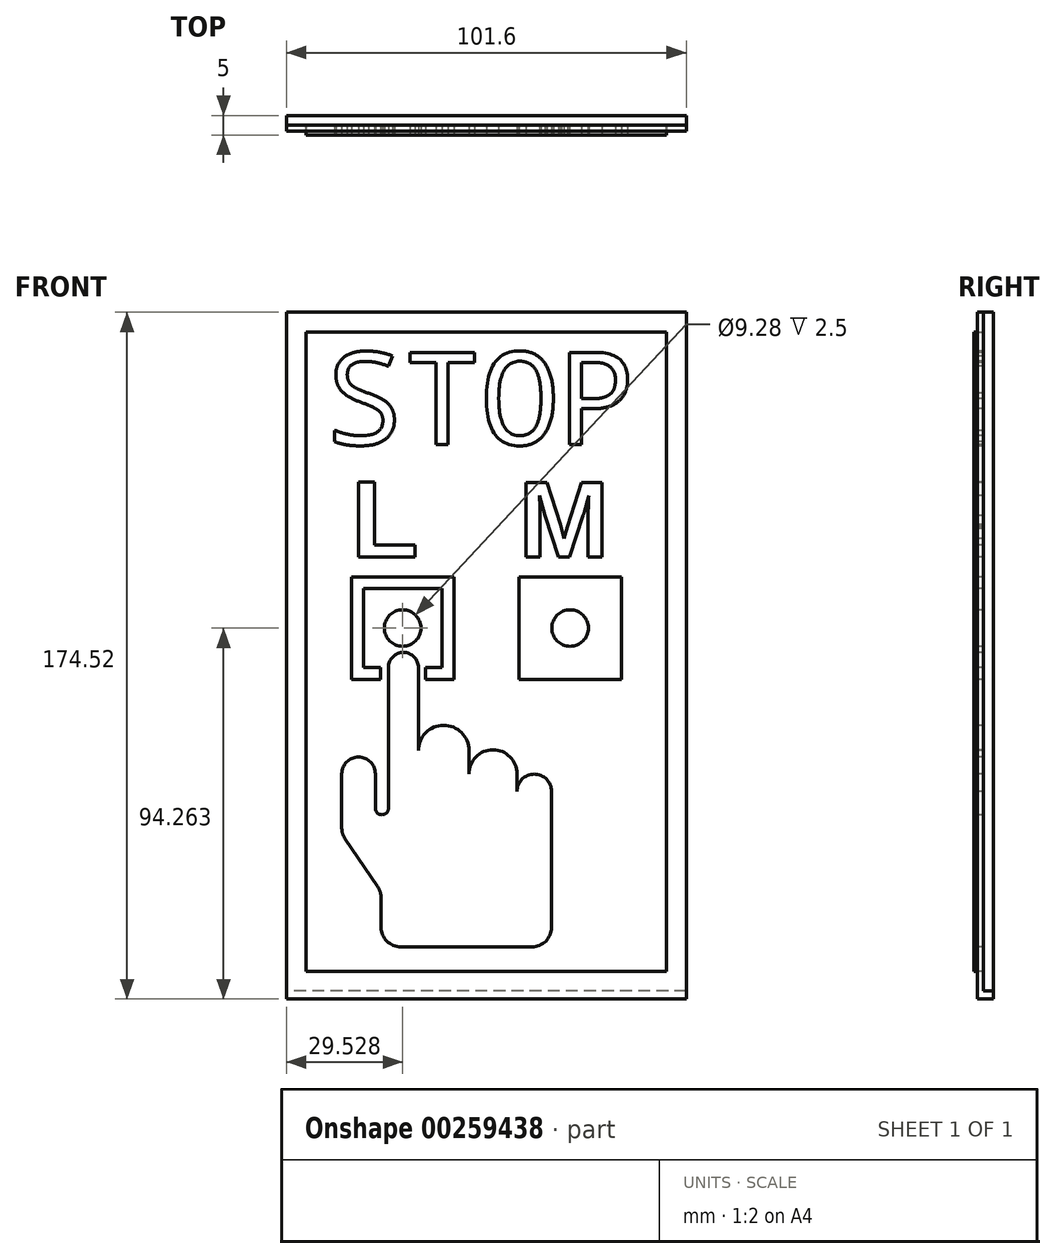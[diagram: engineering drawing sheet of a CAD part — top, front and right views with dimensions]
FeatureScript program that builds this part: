
annotation { "Feature Type Name" : "Feature", "Feature Type Description" : "" }
export const myFeature = defineFeature(function(context is Context, id is Id, definition is map)
    precondition{}
    {
        {
            var Q0;
            Q0=qCreatedBy(makeId("Front.planeOp"),FACE);
            var sketch = newSketch(context, id + "F0", { "sketchPlane" : qUnion([Q0])});
            skLineSegment(sketch, "E0.bottom", {"start": v(0, 0) * mm, "end": v(101.6, 0) * mm});
            skLineSegment(sketch, "E0.top", {"start": v(0, 203.2) * mm, "end": v(101.6, 203.2) * mm});
            skLineSegment(sketch, "E0.left", {"start": v(0, 0) * mm, "end": v(0, 203.2) * mm});
            skLineSegment(sketch, "E0.right", {"start": v(101.6, 0) * mm, "end": v(101.6, 203.2) * mm});
            skLineSegment(sketch, "E1.0", {"start": v(5, 5) * mm, "end": v(5, 198.2) * mm});
            skLineSegment(sketch, "E1.1", {"start": v(5, 5) * mm, "end": v(96.6, 5) * mm});
            skLineSegment(sketch, "E1.2", {"start": v(96.6, 5) * mm, "end": v(96.6, 198.2) * mm});
            skLineSegment(sketch, "E1.3", {"start": v(5, 198.2) * mm, "end": v(96.6, 198.2) * mm});
            skSolve(sketch);
        }
        {
            var Q0;
            Q0=makeQuery(id+"F0.imprint","IMPRINT",FACE,{"disambiguationData":[TD([[makeQuery(id+"F0.imprint","IMPRINT",EDGE,{"derivedFrom":sQuery(id+"F0.wireOp",EDGE,"E1.0")}),-1.0]])]});
            extrude(context, id + "F1", {"entities" : qUnion([Q0]), "depth" : 5 * mm, "offsetDistance" : 25 * mm});
        }
        {
            var Q0;
            Q0=makeQuery(id+"F0.imprint","IMPRINT",FACE,{"disambiguationData":[TD([[makeQuery(id+"F0.imprint","IMPRINT",EDGE,{"derivedFrom":sQuery(id+"F0.wireOp",EDGE,"E0.bottom")}),1.0]])]});
            extrude(context, id + "F2", {"entities" : qUnion([Q0]), "operationType" : NewBodyOperationType.ADD, "depth" : 2.5 * mm, "offsetDistance" : 25 * mm});
        }
        {
            var Q0;
            Q0=makeQuery(id+"F1.opExtrude","CAP_FACE",FACE,{"disambiguationData":[OSD([sQuery(id+"F0.wireOp",EDGE,"E1.0"),sQuery(id+"F0.wireOp",EDGE,"E1.1"),sQuery(id+"F0.wireOp",EDGE,"E1.2"),sQuery(id+"F0.wireOp",EDGE,"E1.3")])],"isStart":false});
            var sketch = newSketch(context, id + "F3", { "sketchPlane" : qUnion([Q0])});
            skLineSegment(sketch, "E2.0", {"start": v(10, 10) * mm, "end": v(10, 193.2) * mm, "construction": true});
            skLineSegment(sketch, "E2.1", {"start": v(10, 10) * mm, "end": v(91.6, 10) * mm, "construction": true});
            skLineSegment(sketch, "E2.2", {"start": v(91.6, 10) * mm, "end": v(91.6, 193.2) * mm, "construction": true});
            skLineSegment(sketch, "E2.3", {"start": v(10, 193.2) * mm, "end": v(91.6, 193.2) * mm, "construction": true});
            skText(sketch, "E3", { "text": "STOP", "fontName": "DroidSansMono.ttf"});
            skLineSegment(sketch, "E4.bottom", {"start": v(19.53, 132.94) * mm, "end": v(39.53, 132.94) * mm});
            skLineSegment(sketch, "E4.top", {"start": v(19.53, 112.94) * mm, "end": v(39.53, 112.94) * mm});
            skLineSegment(sketch, "E4.left", {"start": v(19.53, 132.94) * mm, "end": v(19.53, 112.94) * mm});
            skLineSegment(sketch, "E4.right", {"start": v(39.53, 132.94) * mm, "end": v(39.53, 112.94) * mm});
            skPoint(sketch, "E4.middle", {"position": v(29.53, 122.94) * mm});
            skLineSegment(sketch, "E5.0", {"start": v(16.53, 135.94) * mm, "end": v(42.53, 135.94) * mm});
            skLineSegment(sketch, "E5.1", {"start": v(16.53, 135.94) * mm, "end": v(16.53, 109.94) * mm});
            skLineSegment(sketch, "E5.2", {"start": v(16.53, 109.94) * mm, "end": v(42.53, 109.94) * mm});
            skLineSegment(sketch, "E5.3", {"start": v(42.53, 135.94) * mm, "end": v(42.53, 109.94) * mm});
            skCircle(sketch, "E6", {"center": v(29.53, 122.94) * mm, "radius": 4.64 * mm});
            skLineSegment(sketch, "E7", {"start": v(10, 116.25) * mm, "end": v(10, 95.36) * mm});
            skLineSegment(sketch, "E8", {"start": v(24.06, 54.43) * mm, "end": v(24.06, 46.92) * mm});
            skLineSegment(sketch, "E9", {"start": v(29.06, 41.92) * mm, "end": v(57.08, 41.92) * mm});
            skLineSegment(sketch, "E10", {"start": v(57.08, 41.92) * mm, "end": v(62.35, 41.92) * mm});
            skLineSegment(sketch, "E11", {"start": v(67.35, 46.92) * mm, "end": v(67.35, 81.44) * mm});
            skLineSegment(sketch, "E12", {"start": v(25.91, 112.94) * mm, "end": v(25.91, 77.18) * mm});
            skLineSegment(sketch, "E13", {"start": v(23.19, 57.25) * mm, "end": v(14.93, 69.34) * mm});
            skLineSegment(sketch, "E14", {"start": v(14.06, 72.16) * mm, "end": v(14.06, 85.93) * mm});
            skArc(sketch, "E15", {"start": v(22.59, 85.93) * mm, "mid": v(18.32, 90.2) * mm, "end": v(14.06, 85.93) * mm});
            skLineSegment(sketch, "E16", {"start": v(22.59, 85.93) * mm, "end": v(22.59, 77.18) * mm});
            skArc(sketch, "E17", {"start": v(22.59, 77.18) * mm, "mid": v(24.25, 75.52) * mm, "end": v(25.91, 77.18) * mm});
            skArc(sketch, "E18", {"start": v(33.53, 112.94) * mm, "mid": v(29.72, 116.75) * mm, "end": v(25.91, 112.94) * mm});
            skLineSegment(sketch, "E19", {"start": v(33.53, 112.94) * mm, "end": v(33.53, 91.84) * mm});
            skLineSegment(sketch, "E20", {"start": v(23.9, 112.94) * mm, "end": v(23.9, 109.94) * mm});
            skLineSegment(sketch, "E21", {"start": v(35.28, 112.94) * mm, "end": v(35.28, 109.94) * mm});
            skLineSegment(sketch, "E22", {"start": v(50.8, 169.55) * mm, "end": v(50.8, 115.43) * mm, "construction": true});
            skCircle(sketch, "E23.MirrorC", {"center": v(72.07, 122.94) * mm, "radius": 4.64 * mm});
            skLineSegment(sketch, "E24.MirrorCS", {"start": v(59.07, 135.94) * mm, "end": v(59.07, 109.94) * mm});
            skLineSegment(sketch, "E25.MirrorCS", {"start": v(85.07, 109.94) * mm, "end": v(59.07, 109.94) * mm});
            skLineSegment(sketch, "E26.MirrorCS", {"start": v(85.07, 135.94) * mm, "end": v(85.07, 109.94) * mm});
            skLineSegment(sketch, "E27.MirrorCS", {"start": v(85.07, 135.94) * mm, "end": v(59.07, 135.94) * mm});
            skLineSegment(sketch, "E28.MirrorCS", {"start": v(62.07, 132.94) * mm, "end": v(62.07, 112.94) * mm});
            skLineSegment(sketch, "E29.MirrorCS", {"start": v(82.07, 132.94) * mm, "end": v(82.07, 112.94) * mm});
            skLineSegment(sketch, "E30.MirrorCS", {"start": v(82.07, 112.94) * mm, "end": v(62.07, 112.94) * mm});
            skLineSegment(sketch, "E31.MirrorCS", {"start": v(82.07, 132.94) * mm, "end": v(62.07, 132.94) * mm});
            skLineSegment(sketch, "E32.0", {"start": v(16.53, 140.94) * mm, "end": v(42.53, 140.94) * mm, "construction": true});
            skLineSegment(sketch, "E33.MirrorCS", {"start": v(85.07, 140.94) * mm, "end": v(59.07, 140.94) * mm, "construction": true});
            skText(sketch, "E34", { "text": "L", "fontName": "Arimo-Bold.ttf"});
            skText(sketch, "E35", { "text": "M", "fontName": "Arimo-Bold.ttf"});
            skPoint(sketch, "E36.visualSharp", {"position": v(14.06, 70.62) * mm});
            skArc(sketch, "E36.filletArc", {"start": v(14.06, 72.16) * mm, "mid": v(14.28, 70.69) * mm, "end": v(14.93, 69.34) * mm});
            skPoint(sketch, "E37.visualSharp", {"position": v(24.06, 55.98) * mm});
            skArc(sketch, "E37.filletArc", {"start": v(24.06, 54.43) * mm, "mid": v(23.84, 55.9) * mm, "end": v(23.19, 57.25) * mm});
            skPoint(sketch, "E38.visualSharp", {"position": v(24.06, 41.92) * mm});
            skArc(sketch, "E38.filletArc", {"start": v(24.06, 46.92) * mm, "mid": v(25.52, 43.39) * mm, "end": v(29.06, 41.92) * mm});
            skPoint(sketch, "E39.visualSharp", {"position": v(67.35, 41.92) * mm});
            skArc(sketch, "E39.filletArc", {"start": v(62.35, 41.92) * mm, "mid": v(65.89, 43.39) * mm, "end": v(67.35, 46.92) * mm});
            skArc(sketch, "E40", {"start": v(46.37, 91.84) * mm, "mid": v(39.95, 98.25) * mm, "end": v(33.53, 91.84) * mm});
            skLineSegment(sketch, "E41", {"start": v(46.37, 91.84) * mm, "end": v(46.37, 85.93) * mm});
            skArc(sketch, "E42", {"start": v(58.56, 85.93) * mm, "mid": v(52.46, 92.03) * mm, "end": v(46.37, 85.93) * mm});
            skLineSegment(sketch, "E43", {"start": v(58.56, 85.93) * mm, "end": v(58.56, 81.44) * mm});
            skArc(sketch, "E44", {"start": v(67.35, 81.44) * mm, "mid": v(62.96, 85.83) * mm, "end": v(58.56, 81.44) * mm});
            const initialGuessF3  = {"E3": [0.01, 0.16955, 1, 0, 0.02365], "E34": [0.01653, 0.14094, 1, 0, 0.01996], "E35": [0.05907, 0.14094, 1, 0, 0.01986]};
            skSetInitialGuess(sketch, initialGuessF3);
            skSolve(sketch);
        }
        {
            var Q0;
            Q0=makeQuery(id+"F3.imprint","IMPRINT",FACE,{"disambiguationData":[TD([[makeQuery(id+"F3.imprint","IMPRINT",EDGE,{"derivedFrom":sQuery(id+"F3.wireOp",EDGE,"E3.sketch_text.stroke-0")}),-1.0]])]});
            var Q1;
            Q1=makeQuery(id+"F3.imprint","IMPRINT",FACE,{"disambiguationData":[TD([[makeQuery(id+"F3.imprint","IMPRINT",EDGE,{"derivedFrom":sQuery(id+"F3.wireOp",EDGE,"E3.sketch_text.stroke-20")}),-1.0]])]});
            var Q2;
            Q2=makeQuery(id+"F3.imprint","IMPRINT",FACE,{"disambiguationData":[TD([[makeQuery(id+"F3.imprint","IMPRINT",EDGE,{"derivedFrom":sQuery(id+"F3.wireOp",EDGE,"bff1b2f7-5b43-40db-ad50-737210fc3e16.sketch_text.stroke-0")}),-1.0]])]});
            var Q3;
            Q3=makeQuery(id+"F3.imprint","IMPRINT",FACE,{"disambiguationData":[TD([[makeQuery(id+"F3.imprint","IMPRINT",EDGE,{"derivedFrom":sQuery(id+"F3.wireOp",EDGE,"bff1b2f7-5b43-40db-ad50-737210fc3e16.sketch_text.stroke-35")}),-1.0]])]});
            var Q4;
            Q4=makeQuery(id+"F3.imprint","IMPRINT",FACE,{"disambiguationData":[TD([[makeQuery(id+"F3.imprint","IMPRINT",EDGE,{"derivedFrom":sQuery(id+"F3.wireOp",EDGE,"bff1b2f7-5b43-40db-ad50-737210fc3e16.sketch_text.stroke-60")}),-1.0]])]});
            var Q5;
            Q5=makeQuery(id+"F3.imprint","IMPRINT",FACE,{"disambiguationData":[TD([[makeQuery(id+"F3.imprint","IMPRINT",EDGE,{"derivedFrom":sQuery(id+"F3.wireOp",EDGE,"bff1b2f7-5b43-40db-ad50-737210fc3e16.sketch_text.stroke-72")}),-1.0]])]});
            var Q6;
            Q6=makeQuery(id+"F3.imprint","IMPRINT",FACE,{"disambiguationData":[TD([[makeQuery(id+"F3.imprint","IMPRINT",EDGE,{"derivedFrom":sQuery(id+"F3.wireOp",EDGE,"E3.sketch_text.stroke-28")}),-1.0]])]});
            var Q7;
            Q7=makeQuery(id+"F3.imprint","IMPRINT",FACE,{"disambiguationData":[TD([[makeQuery(id+"F3.imprint","IMPRINT",EDGE,{"derivedFrom":sQuery(id+"F3.wireOp",EDGE,"E3.sketch_text.stroke-40")}),-1.0]])]});
            var Q8;
            Q8=makeQuery(id+"F3.imprint","IMPRINT",FACE,{"disambiguationData":[TD([[makeQuery(id+"F3.imprint","IMPRINT",EDGE,{"derivedFrom":sQuery(id+"F3.wireOp",EDGE,"E8")}),1.0]])]});
            var Q9;
            Q9=makeQuery(id+"F3.imprint","IMPRINT",FACE,{"disambiguationData":[TD([[makeQuery(id+"F3.imprint","IMPRINT",EDGE,{"derivedFrom":sQuery(id+"F3.wireOp",EDGE,"bff1b2f7-5b43-40db-ad50-737210fc3e16.sketch_text.stroke-20")}),-1.0]])]});
            var Q10;
            Q10=makeQuery(id+"F3.imprint","IMPRINT",FACE,{"disambiguationData":[TD([[makeQuery(id+"F3.imprint","IMPRINT",EDGE,{"derivedFrom":sQuery(id+"F3.wireOp",EDGE,"bff1b2f7-5b43-40db-ad50-737210fc3e16.sketch_text.stroke-45")}),-1.0]])]});
            var Q11;
            Q11=makeQuery(id+"F3.imprint","IMPRINT",FACE,{"disambiguationData":[TD([[makeQuery(id+"F3.imprint","IMPRINT",EDGE,{"derivedFrom":sQuery(id+"F3.wireOp",EDGE,"E4.bottom")}),1.0]])]});
            var Q12;
            {var subQ1=sQuery(id+"F3.wireOp",EDGE,"E12");var subQ6=sQuery(id+"F3.wireOp",EDGE,"E5.2");var subQ7=makeQuery(id+"F3.imprint","INTERSECT",VERTEX,{"derivedFrom":[subQ6,subQ1]});Q12=makeQuery(id+"F3.imprint","IMPRINT",FACE,{"disambiguationData":[TD([[makeQuery(id+"F3.imprint","IMPRINT",EDGE,{"disambiguationData":[TD([[subQ7,-1.0]])],"derivedFrom":subQ6}),1.0]])]});}
            var Q13;
            Q13=makeQuery(id+"F3.imprint","IMPRINT",FACE,{"disambiguationData":[TD([[makeQuery(id+"F3.imprint","IMPRINT",EDGE,{"derivedFrom":sQuery(id+"F3.wireOp",EDGE,"E6")}),1.0]])]});
            var Q14;
            {var subQ0=sQuery(id+"F3.wireOp",EDGE,"E18");Q14=makeQuery(id+"F3.imprint","IMPRINT",FACE,{"disambiguationData":[TD([[makeQuery(id+"F3.imprint","IMPRINT",EDGE,{"derivedFrom":subQ0}),1.0]])]});}
            var Q15;
            Q15=makeQuery(id+"F3.imprint","IMPRINT",FACE,{"disambiguationData":[TD([[makeQuery(id+"F3.imprint","IMPRINT",EDGE,{"derivedFrom":sQuery(id+"F3.wireOp",EDGE,"E24.MirrorCS")}),1.0]])]});
            var Q16;
            Q16=makeQuery(id+"F3.imprint","IMPRINT",FACE,{"disambiguationData":[TD([[makeQuery(id+"F3.imprint","IMPRINT",EDGE,{"derivedFrom":sQuery(id+"F3.wireOp",EDGE,"E23.MirrorC")}),-1.0]])]});
            var Q17;
            Q17=makeQuery(id+"F3.imprint","IMPRINT",FACE,{"disambiguationData":[TD([[makeQuery(id+"F3.imprint","IMPRINT",EDGE,{"derivedFrom":sQuery(id+"F3.wireOp",EDGE,"E34.sketch_text.stroke-0")}),-1.0]])]});
            var Q18;
            Q18=makeQuery(id+"F3.imprint","IMPRINT",FACE,{"disambiguationData":[TD([[makeQuery(id+"F3.imprint","IMPRINT",EDGE,{"derivedFrom":sQuery(id+"F3.wireOp",EDGE,"E35.sketch_text.stroke-0")}),-1.0]])]});
            extrude(context, id + "F4", {"entities" : qUnion([Q0, Q1, Q2, Q3, Q4, Q5, Q6, Q7, Q8, Q9, Q10, Q11, Q12, Q13, Q14, Q15, Q16, Q17, Q18]), "operationType" : NewBodyOperationType.REMOVE, "oppositeDirection" : true, "depth" : 2.5 * mm, "offsetDistance" : 25 * mm});
        }
        {
            var Q0;
            {var subQ7=sQuery(id+"F0.wireOp",EDGE,"E1.1");var subQ8=sQuery(id+"F0.wireOp",EDGE,"E1.0");var subQ10=sQuery(id+"F0.wireOp",EDGE,"E1.2");var subQ11=sQuery(id+"F0.wireOp",EDGE,"E1.3");Q0=makeQuery(id+"F4.boolean.opBoolean","SPLIT",FACE,{"disambiguationData":[TD([makeQuery(id+"F1.opExtrude","SWEPT_FACE",FACE,{"disambiguationData":[OSD([subQ8])]})])],"derivedFrom":makeQuery(id+"F1.opExtrude","CAP_FACE",FACE,{"disambiguationData":[OSD([subQ8,subQ7,subQ10,subQ11])],"isStart":false})});}
            var sketch = newSketch(context, id + "F5", { "sketchPlane" : qUnion([Q0])});
            skLineSegment(sketch, "E45", {"start": v(0, 35.74) * mm, "end": v(102.67, 35.74) * mm});
            skLineSegment(sketch, "E46", {"start": v(102.67, 35.74) * mm, "end": v(102.67, 0) * mm});
            skLineSegment(sketch, "E47", {"start": v(102.67, 0) * mm, "end": v(-3.36, 0) * mm});
            skLineSegment(sketch, "E48", {"start": v(-3.36, 0) * mm, "end": v(0, 35.74) * mm});
            skSolve(sketch);
        }
        {
            var Q0;
            Q0=qSketchRegion(id+"F5",true);
            extrude(context, id + "F6", {"entities" : qUnion([Q0]), "operationType" : NewBodyOperationType.REMOVE, "oppositeDirection" : true, "depth" : 2.5 * mm, "offsetDistance" : 25 * mm});
        }
        {
            var Q0;
            Q0=makeQuery(id+"F6.boolean.opBoolean","MERGE",FACE,{"derivedFrom":[makeQuery(id+"F2.opExtrude","CAP_FACE",FACE,{"disambiguationData":[OSD([sQuery(id+"F0.wireOp",EDGE,"E0.bottom"),sQuery(id+"F0.wireOp",EDGE,"E0.top"),sQuery(id+"F0.wireOp",EDGE,"E0.left"),sQuery(id+"F0.wireOp",EDGE,"E0.right"),sQuery(id+"F0.wireOp",EDGE,"E1.0"),sQuery(id+"F0.wireOp",EDGE,"E1.1"),sQuery(id+"F0.wireOp",EDGE,"E1.2"),sQuery(id+"F0.wireOp",EDGE,"E1.3")])],"isStart":false}),makeQuery(id+"F6.opExtrude","CAP_FACE",FACE,{"disambiguationData":[OSD([sQuery(id+"F5.wireOp",EDGE,"E45"),sQuery(id+"F5.wireOp",EDGE,"E46"),sQuery(id+"F5.wireOp",EDGE,"E47"),sQuery(id+"F5.wireOp",EDGE,"E48")])],"isStart":false})]});
            var sketch = newSketch(context, id + "F7", { "sketchPlane" : qUnion([Q0])});
            skLineSegment(sketch, "E49", {"start": v(5, 35.74) * mm, "end": v(5, 30.74) * mm});
            skLineSegment(sketch, "E50", {"start": v(5, 30.74) * mm, "end": v(0, 30.74) * mm});
            skLineSegment(sketch, "E51", {"start": v(0, 30.74) * mm, "end": v(0, 0) * mm});
            skLineSegment(sketch, "E52", {"start": v(0, 0) * mm, "end": v(101.6, 0) * mm});
            skLineSegment(sketch, "E53", {"start": v(101.6, 0) * mm, "end": v(101.6, 30.74) * mm});
            skLineSegment(sketch, "E54", {"start": v(101.6, 30.74) * mm, "end": v(5, 30.74) * mm});
            skSolve(sketch);
        }
        {
            var Q0;
            Q0=qSketchRegion(id+"F7",true);
            extrude(context, id + "F8", {"entities" : qUnion([Q0]), "operationType" : NewBodyOperationType.REMOVE, "endBound" : BoundingType.THROUGH_ALL, "oppositeDirection" : true, "depth" : 25 * mm, "offsetDistance" : 25 * mm, "hasSecondDirection" : true, "secondDirectionBound" : BoundingType.THROUGH_ALL, "secondDirectionOppositeDirection" : false, "secondDirectionDepth" : 25 * mm});
        }
        {
            var Q0;
            Q0=makeQuery(id+"F0.imprint","IMPRINT",FACE,{"disambiguationData":[TD([[makeQuery(id+"F0.imprint","IMPRINT",EDGE,{"derivedFrom":sQuery(id+"F0.wireOp",EDGE,"E0.bottom")}),1.0]])]});
            var Q1;
            Q1=makeQuery(id+"F0.imprint","IMPRINT",FACE,{"disambiguationData":[TD([[makeQuery(id+"F0.imprint","IMPRINT",EDGE,{"derivedFrom":sQuery(id+"F0.wireOp",EDGE,"E1.0")}),-1.0]])]});
            extrude(context, id + "F9", {"entities" : qUnion([Q0, Q1]), "depth" : 4 * mm, "offsetDistance" : 25 * mm});
        }
        {
            var Q0;
            Q0=makeQuery(id+"F9.opExtrude","CAP_FACE",FACE,{"disambiguationData":[OSD([sQuery(id+"F0.wireOp",EDGE,"E0.bottom"),sQuery(id+"F0.wireOp",EDGE,"E0.top"),sQuery(id+"F0.wireOp",EDGE,"E0.left"),sQuery(id+"F0.wireOp",EDGE,"E0.right")])],"isStart":false});
            var sketch = newSketch(context, id + "F10", { "sketchPlane" : qUnion([Q0])});
            skLineSegment(sketch, "E55.bottom", {"start": v(0, 0) * mm, "end": v(101.6, 0) * mm});
            skLineSegment(sketch, "E55.top", {"start": v(0, 28.68) * mm, "end": v(101.6, 28.68) * mm});
            skLineSegment(sketch, "E55.left", {"start": v(0, 0) * mm, "end": v(0, 28.68) * mm});
            skLineSegment(sketch, "E55.right", {"start": v(101.6, 0) * mm, "end": v(101.6, 28.68) * mm});
            skSolve(sketch);
        }
        {
            var Q0;
            Q0=qSketchRegion(id+"F10",true);
            extrude(context, id + "F11", {"entities" : qUnion([Q0]), "operationType" : NewBodyOperationType.REMOVE, "oppositeDirection" : true, "depth" : 25 * mm, "offsetDistance" : 25 * mm});
        }
    });
